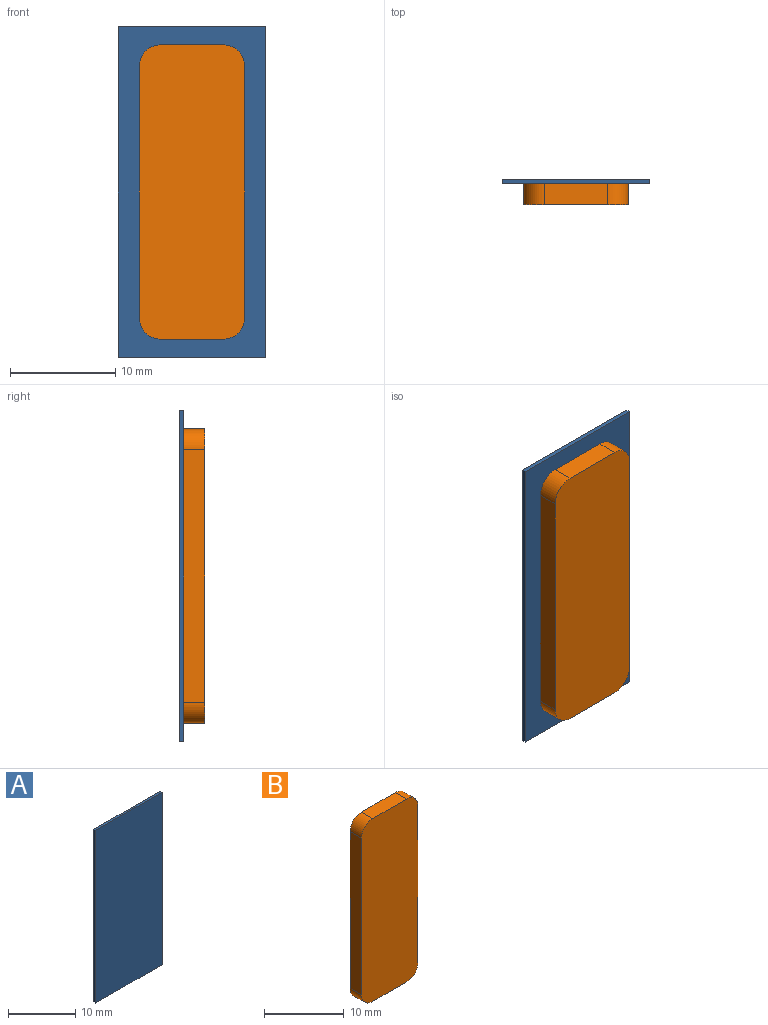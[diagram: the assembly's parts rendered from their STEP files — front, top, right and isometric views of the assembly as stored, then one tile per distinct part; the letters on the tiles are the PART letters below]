
ASSEMBLY  parts=2 mates=1
PART A: 6 faces, bbox 14x0.4x31.5 mm
  f0: plane 31.5x0.4mm, normal (1,0,0), area 12.6mm2, adj f1,f3,f4,f5
  f1: plane 14x0.4mm, normal (0,0,1), area 5.6mm2, adj f0,f2,f4,f5
  f2: plane 31.5x0.4mm, normal (-1,0,0), area 12.6mm2, adj f1,f3,f4,f5
  f3: plane 14x0.4mm, normal (0,0,-1), area 5.6mm2, adj f0,f2,f4,f5
  f4: plane 31.5x14mm, normal (0,1,0), area 441mm2, adj f0,f1,f2,f3
  f5: plane 31.5x14mm, normal (0,-1,0), area 441mm2, adj f0,f1,f2,f3
PART B: 10 faces, bbox 10x2x28 mm
  f0: plane 24x2mm, normal (-1,0,0), area 48mm2, adj f1,f7,f8,f9
  f1: cylinder r=2mm len=2mm, axis (0,1,0), area 6.3mm2, adj f0,f2,f8,f9
  f2: plane 6x2mm, normal (0,0,-1), area 12mm2, adj f1,f3,f8,f9
  f3: cylinder r=2mm len=2mm, axis (0,1,0), area 6.3mm2, adj f2,f4,f8,f9
  f4: plane 24x2mm, normal (1,0,0), area 48mm2, adj f3,f5,f8,f9
  f5: cylinder r=2mm len=2mm, axis (0,1,0), area 6.3mm2, adj f4,f6,f8,f9
  f6: plane 6x2mm, normal (0,0,1), area 12mm2, adj f5,f7,f8,f9
  f7: cylinder r=2mm len=2mm, axis (0,1,0), area 6.3mm2, adj f0,f6,f8,f9
  f8: plane 28x10mm, normal (0,-1,0), area 276.6mm2, adj f0,f1,f2,f3,f4,f5,f6,f7
  f9: plane 28x10mm, normal (0,1,0), area 276.6mm2, adj f0,f1,f2,f3,f4,f5,f6,f7
PLACE A t=(-13.06,-16.35,0.54)mm
PLACE B t=(-13.06,-16.35,0.54)mm
MATE fastened A.f5 <-> B.f9  axis (0,-1,0) through (-13.06,-16.35,0.54)mm
